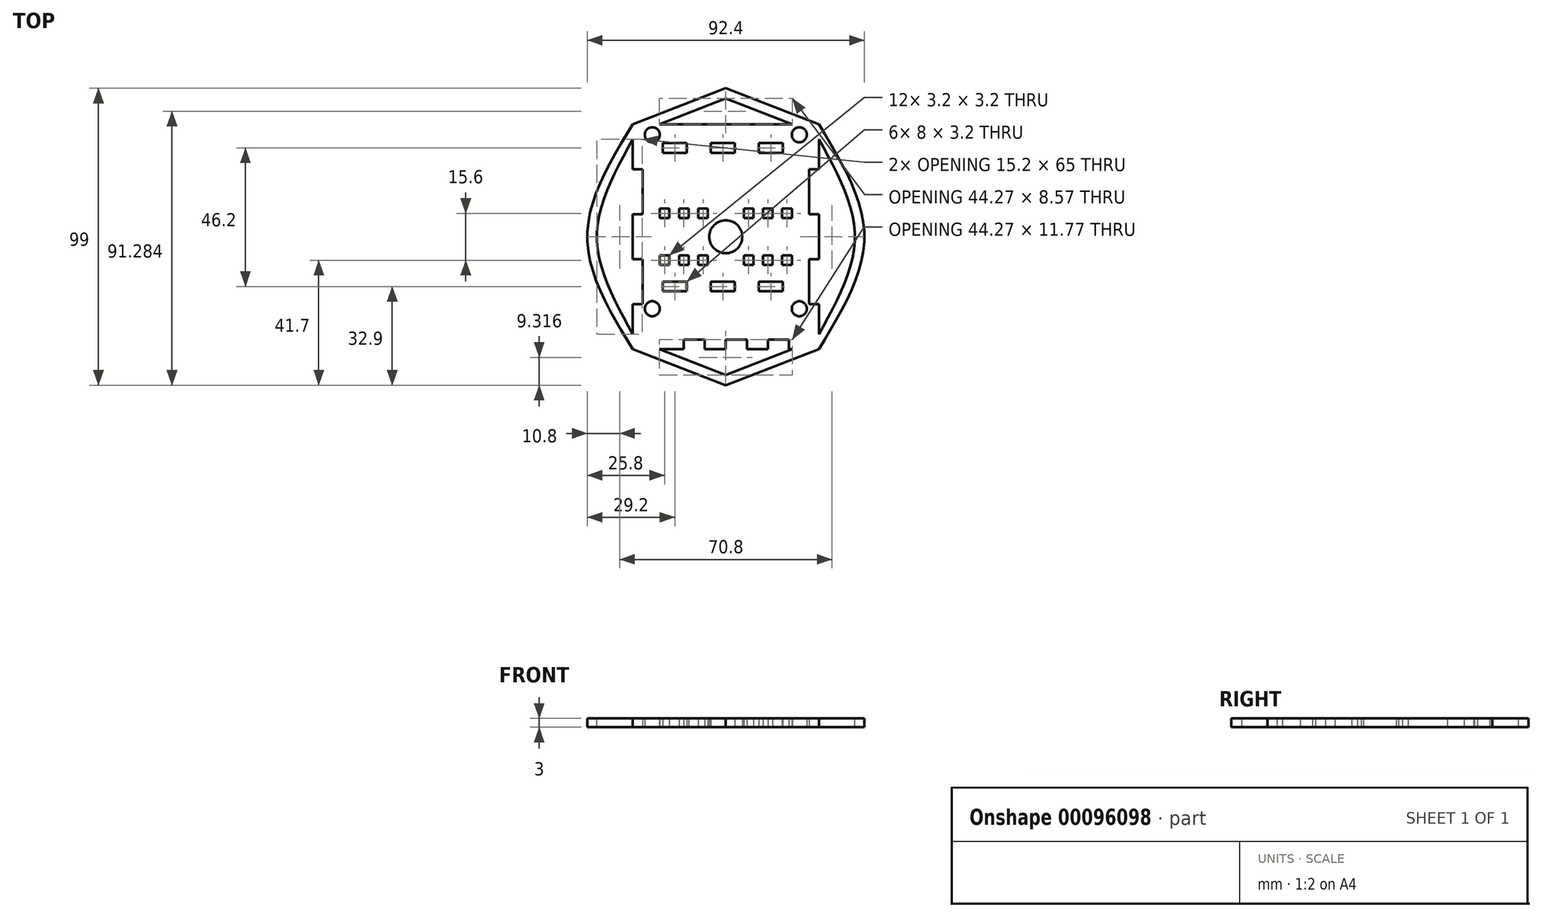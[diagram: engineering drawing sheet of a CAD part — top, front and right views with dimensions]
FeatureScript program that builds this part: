
annotation { "Feature Type Name" : "Feature", "Feature Type Description" : "" }
export const myFeature = defineFeature(function(context is Context, id is Id, definition is map)
    precondition{}
    {
        {
            var Q0;
            Q0=qCreatedBy(makeId("Top.planeOp"),FACE);
            var sketch = newSketch(context, id + "F0", { "sketchPlane" : qUnion([Q0])});
            skLineSegment(sketch, "E0.top", {"start": v(0, 37.5) * mm, "end": v(-22.14, 37.5) * mm});
            skLineSegment(sketch, "E0.right", {"start": v(-31, -32.5) * mm, "end": v(-31, -22.5) * mm});
            skPoint(sketch, "E0.middle", {"position": v(0, 0) * mm});
            skLineSegment(sketch, "E1", {"start": v(-31, 22.5) * mm, "end": v(-27.8, 22.5) * mm});
            skLineSegment(sketch, "E2", {"start": v(-27.8, 22.5) * mm, "end": v(-27.8, 7.5) * mm});
            skLineSegment(sketch, "E3", {"start": v(-27.8, 7.5) * mm, "end": v(-31, 7.5) * mm});
            skLineSegment(sketch, "E4", {"start": v(-31, 7.5) * mm, "end": v(-31, -7.5) * mm});
            skLineSegment(sketch, "E5", {"start": v(-31, -7.5) * mm, "end": v(-27.8, -7.5) * mm});
            skLineSegment(sketch, "E6", {"start": v(-27.8, -7.5) * mm, "end": v(-27.8, -22.5) * mm});
            skLineSegment(sketch, "E7", {"start": v(-27.8, -22.5) * mm, "end": v(-31, -22.5) * mm});
            skLineSegment(sketch, "E8", {"start": v(-31, -22.5) * mm, "end": v(-31, -32.5) * mm});
            skLineSegment(sketch, "E9", {"start": v(27.8, 22.5) * mm, "end": v(31, 22.5) * mm});
            skLineSegment(sketch, "E10", {"start": v(31, 7.5) * mm, "end": v(27.8, 7.5) * mm});
            skLineSegment(sketch, "E11", {"start": v(27.8, -7.5) * mm, "end": v(31, -7.5) * mm});
            skLineSegment(sketch, "E12", {"start": v(31, -22.5) * mm, "end": v(27.8, -22.5) * mm});
            skLineSegment(sketch, "E13.trimOffspring", {"start": v(-31, 22.5) * mm, "end": v(-31, 32.5) * mm});
            skLineSegment(sketch, "E14.trimOffspring", {"start": v(-31, -7.5) * mm, "end": v(-31, 7.5) * mm});
            skCircle(sketch, "E15", {"center": v(0, 0) * mm, "radius": 5.5 * mm});
            skLineSegment(sketch, "E16", {"start": v(0, 0) * mm, "end": v(5.5, 0) * mm, "construction": true});
            skLineSegment(sketch, "E17", {"start": v(-31, 0) * mm, "end": v(0, 0) * mm, "construction": true});
            skLineSegment(sketch, "E18", {"start": v(0, -14.47) * mm, "end": v(0, 12.75) * mm, "construction": true});
            skLineSegment(sketch, "E19", {"start": v(5.5, 0) * mm, "end": v(6, 0) * mm, "construction": true});
            skLineSegment(sketch, "E20", {"start": v(6, 0) * mm, "end": v(6, 9.4) * mm, "construction": true});
            skLineSegment(sketch, "E21.bottom", {"start": v(6, 9.4) * mm, "end": v(9.2, 9.4) * mm});
            skLineSegment(sketch, "E21.top", {"start": v(6, 6.2) * mm, "end": v(9.2, 6.2) * mm});
            skLineSegment(sketch, "E21.left", {"start": v(6, 9.4) * mm, "end": v(6, 6.2) * mm});
            skLineSegment(sketch, "E21.right", {"start": v(9.2, 9.4) * mm, "end": v(9.2, 6.2) * mm});
            skLineSegment(sketch, "E22", {"start": v(6, 0) * mm, "end": v(12.4, 0) * mm, "construction": true});
            skLineSegment(sketch, "E23", {"start": v(12.4, 0) * mm, "end": v(12.4, 9.4) * mm, "construction": true});
            skLineSegment(sketch, "E24", {"start": v(12.4, 0) * mm, "end": v(18.8, 0) * mm, "construction": true});
            skLineSegment(sketch, "E25", {"start": v(18.8, 0) * mm, "end": v(18.8, 9.4) * mm, "construction": true});
            skLineSegment(sketch, "E26", {"start": v(18.8, 0) * mm, "end": v(24, 0) * mm, "construction": true});
            skLineSegment(sketch, "E27.bottom", {"start": v(12.4, 9.4) * mm, "end": v(15.6, 9.4) * mm});
            skLineSegment(sketch, "E27.top", {"start": v(12.4, 6.2) * mm, "end": v(15.6, 6.2) * mm});
            skLineSegment(sketch, "E27.left", {"start": v(12.4, 9.4) * mm, "end": v(12.4, 6.2) * mm});
            skLineSegment(sketch, "E27.right", {"start": v(15.6, 9.4) * mm, "end": v(15.6, 6.2) * mm});
            skLineSegment(sketch, "E28.bottom", {"start": v(18.8, 9.4) * mm, "end": v(22, 9.4) * mm});
            skLineSegment(sketch, "E28.top", {"start": v(18.8, 6.2) * mm, "end": v(22, 6.2) * mm});
            skLineSegment(sketch, "E28.left", {"start": v(18.8, 9.4) * mm, "end": v(18.8, 6.2) * mm});
            skLineSegment(sketch, "E28.right", {"start": v(22, 9.4) * mm, "end": v(22, 6.2) * mm});
            skLineSegment(sketch, "E29.MirrorCS", {"start": v(-5.5, 0) * mm, "end": v(-6, 0) * mm, "construction": true});
            skLineSegment(sketch, "E30.MirrorCS", {"start": v(-6, 0) * mm, "end": v(-12.4, 0) * mm, "construction": true});
            skLineSegment(sketch, "E31.MirrorCS", {"start": v(-18.8, 0) * mm, "end": v(-24, 0) * mm, "construction": true});
            skLineSegment(sketch, "E32.MirrorCS", {"start": v(-12.4, 0) * mm, "end": v(-18.8, 0) * mm, "construction": true});
            skLineSegment(sketch, "E33", {"start": v(-31, 0) * mm, "end": v(27.8, 0) * mm, "construction": true});
            skLineSegment(sketch, "E34.MirrorCS", {"start": v(0, 0) * mm, "end": v(0, 30) * mm, "construction": true});
            skLineSegment(sketch, "E35.MirrorCS", {"start": v(6, -9.4) * mm, "end": v(9.2, -9.4) * mm});
            skLineSegment(sketch, "E36.MirrorCS", {"start": v(12.4, -9.4) * mm, "end": v(12.4, -6.2) * mm});
            skLineSegment(sketch, "E37.MirrorCS", {"start": v(18.8, -9.4) * mm, "end": v(18.8, -6.2) * mm});
            skLineSegment(sketch, "E38.MirrorCS", {"start": v(6, -9.4) * mm, "end": v(6, -6.2) * mm});
            skLineSegment(sketch, "E39.MirrorCS", {"start": v(18.8, -9.4) * mm, "end": v(22, -9.4) * mm});
            skLineSegment(sketch, "E40.MirrorCS", {"start": v(6, -6.2) * mm, "end": v(9.2, -6.2) * mm});
            skLineSegment(sketch, "E41.MirrorCS", {"start": v(12.4, 0) * mm, "end": v(12.4, -9.4) * mm, "construction": true});
            skLineSegment(sketch, "E42.MirrorCS", {"start": v(9.2, -9.4) * mm, "end": v(9.2, -6.2) * mm});
            skLineSegment(sketch, "E43.MirrorCS", {"start": v(15.6, -9.4) * mm, "end": v(15.6, -6.2) * mm});
            skLineSegment(sketch, "E44.MirrorCS", {"start": v(12.4, -6.2) * mm, "end": v(15.6, -6.2) * mm});
            skLineSegment(sketch, "E45.MirrorCS", {"start": v(12.4, -9.4) * mm, "end": v(15.6, -9.4) * mm});
            skLineSegment(sketch, "E46.MirrorCS", {"start": v(18.8, 0) * mm, "end": v(18.8, -9.4) * mm, "construction": true});
            skLineSegment(sketch, "E47.MirrorCS", {"start": v(18.8, -6.2) * mm, "end": v(22, -6.2) * mm});
            skLineSegment(sketch, "E48.MirrorCS", {"start": v(22, -9.4) * mm, "end": v(22, -6.2) * mm});
            skLineSegment(sketch, "E49.MirrorCS", {"start": v(6, 0) * mm, "end": v(6, -9.4) * mm, "construction": true});
            skLineSegment(sketch, "E50.MirrorCS", {"start": v(-9.2, 9.4) * mm, "end": v(-9.2, 6.2) * mm});
            skLineSegment(sketch, "E51.MirrorCS", {"start": v(-15.6, 9.4) * mm, "end": v(-15.6, 6.2) * mm});
            skLineSegment(sketch, "E52.MirrorCS", {"start": v(-12.4, 9.4) * mm, "end": v(-15.6, 9.4) * mm});
            skLineSegment(sketch, "E53.MirrorCS", {"start": v(-18.8, 6.2) * mm, "end": v(-22, 6.2) * mm});
            skLineSegment(sketch, "E54.MirrorCS", {"start": v(-18.8, 9.4) * mm, "end": v(-18.8, 6.2) * mm});
            skLineSegment(sketch, "E55.MirrorCS", {"start": v(-6, 9.4) * mm, "end": v(-9.2, 9.4) * mm});
            skLineSegment(sketch, "E56.MirrorCS", {"start": v(-22, 9.4) * mm, "end": v(-22, 6.2) * mm});
            skLineSegment(sketch, "E57.MirrorCS", {"start": v(-18.8, 9.4) * mm, "end": v(-22, 9.4) * mm});
            skLineSegment(sketch, "E58.MirrorCS", {"start": v(-6, 6.2) * mm, "end": v(-9.2, 6.2) * mm});
            skLineSegment(sketch, "E59.MirrorCS", {"start": v(-12.4, 9.4) * mm, "end": v(-12.4, 6.2) * mm});
            skLineSegment(sketch, "E60.MirrorCS", {"start": v(-12.4, 6.2) * mm, "end": v(-15.6, 6.2) * mm});
            skLineSegment(sketch, "E61.MirrorCS", {"start": v(-6, 9.4) * mm, "end": v(-6, 6.2) * mm});
            skLineSegment(sketch, "E62.MirrorCS", {"start": v(-18.8, -9.4) * mm, "end": v(-18.8, -6.2) * mm});
            skLineSegment(sketch, "E63.MirrorCS", {"start": v(-12.4, -9.4) * mm, "end": v(-12.4, -6.2) * mm});
            skLineSegment(sketch, "E64.MirrorCS", {"start": v(-6, -9.4) * mm, "end": v(-6, -6.2) * mm});
            skLineSegment(sketch, "E65.MirrorCS", {"start": v(-12.4, -9.4) * mm, "end": v(-15.6, -9.4) * mm});
            skLineSegment(sketch, "E66.MirrorCS", {"start": v(-18.8, -6.2) * mm, "end": v(-22, -6.2) * mm});
            skLineSegment(sketch, "E67.MirrorCS", {"start": v(-18.8, -9.4) * mm, "end": v(-22, -9.4) * mm});
            skLineSegment(sketch, "E68.MirrorCS", {"start": v(-12.4, -6.2) * mm, "end": v(-15.6, -6.2) * mm});
            skLineSegment(sketch, "E69.MirrorCS", {"start": v(-12.4, 0) * mm, "end": v(-12.4, -9.4) * mm, "construction": true});
            skLineSegment(sketch, "E70.MirrorCS", {"start": v(-18.8, 0) * mm, "end": v(-18.8, -9.4) * mm, "construction": true});
            skLineSegment(sketch, "E71.MirrorCS", {"start": v(-6, -9.4) * mm, "end": v(-9.2, -9.4) * mm});
            skLineSegment(sketch, "E72.MirrorCS", {"start": v(-6, 0) * mm, "end": v(-6, -9.4) * mm, "construction": true});
            skLineSegment(sketch, "E73.MirrorCS", {"start": v(-22, -9.4) * mm, "end": v(-22, -6.2) * mm});
            skLineSegment(sketch, "E74.MirrorCS", {"start": v(-9.2, -9.4) * mm, "end": v(-9.2, -6.2) * mm});
            skLineSegment(sketch, "E75.MirrorCS", {"start": v(-6, -6.2) * mm, "end": v(-9.2, -6.2) * mm});
            skLineSegment(sketch, "E76.MirrorCS", {"start": v(-15.6, -9.4) * mm, "end": v(-15.6, -6.2) * mm});
            skLineSegment(sketch, "E77", {"start": v(31, 32.5) * mm, "end": v(31, 22.5) * mm});
            skLineSegment(sketch, "E78", {"start": v(27.8, 22.5) * mm, "end": v(27.8, 7.5) * mm});
            skLineSegment(sketch, "E79", {"start": v(27.8, -7.5) * mm, "end": v(27.8, -22.5) * mm});
            skLineSegment(sketch, "E80.trimOffspring", {"start": v(31, -22.5) * mm, "end": v(31, -32.5) * mm});
            skLineSegment(sketch, "E81", {"start": v(31, 7.5) * mm, "end": v(31, -7.5) * mm});
            skLineSegment(sketch, "E82", {"start": v(31, 22.5) * mm, "end": v(34.2, 22.5) * mm});
            skLineSegment(sketch, "E83", {"start": v(0, 37.5) * mm, "end": v(0, 49.5) * mm, "construction": true});
            skPoint(sketch, "E83.startSnap0", {"position": v(0, 15) * mm});
            skLineSegment(sketch, "E84", {"start": v(0, 43.5) * mm, "end": v(34.2, 43.5) * mm, "construction": true});
            skLineSegment(sketch, "E85", {"start": v(0, 43.5) * mm, "end": v(-40.16, 43.5) * mm, "construction": true});
            skLineSegment(sketch, "E86", {"start": v(34.2, 37.5) * mm, "end": v(34.2, 43.5) * mm, "construction": true});
            skLineSegment(sketch, "E87", {"start": v(-31, 0) * mm, "end": v(-43, 0) * mm, "construction": true});
            skLineSegment(sketch, "E88", {"start": v(-27.8, 15) * mm, "end": v(-54.38, 15) * mm, "construction": true});
            skLineSegment(sketch, "E89", {"start": v(-27.8, -15) * mm, "end": v(-55.02, -15) * mm, "construction": true});
            skLineSegment(sketch, "E90", {"start": v(-31, 0) * mm, "end": v(-31, -20) * mm, "construction": true});
            skLineSegment(sketch, "E91", {"start": v(-31, 0) * mm, "end": v(-31, 20) * mm, "construction": true});
            skLineSegment(sketch, "E92", {"start": v(-31, 20) * mm, "end": v(-43, 20) * mm, "construction": true});
            skLineSegment(sketch, "E93", {"start": v(-43, 20) * mm, "end": v(-43, -20) * mm, "construction": true});
            skLineSegment(sketch, "E94", {"start": v(-31, -32.5) * mm, "end": v(-31, -28.4) * mm, "construction": true});
            skLineSegment(sketch, "E95", {"start": v(-21, -37.5) * mm, "end": v(-22.14, -37.5) * mm, "construction": true});
            skLineSegment(sketch, "E96", {"start": v(-22.14, -37.5) * mm, "end": v(-21, -37.5) * mm});
            skLineSegment(sketch, "E97", {"start": v(22.14, -37.5) * mm, "end": v(21, -37.5) * mm});
            skLineSegment(sketch, "E98", {"start": v(21, -37.5) * mm, "end": v(21, -34.3) * mm});
            skLineSegment(sketch, "E99", {"start": v(21, -34.3) * mm, "end": v(14, -34.3) * mm});
            skLineSegment(sketch, "E100", {"start": v(14, -34.3) * mm, "end": v(14, -37.5) * mm});
            skLineSegment(sketch, "E101", {"start": v(14, -37.5) * mm, "end": v(7, -37.5) * mm});
            skLineSegment(sketch, "E102", {"start": v(7, -37.5) * mm, "end": v(7, -34.3) * mm});
            skLineSegment(sketch, "E103", {"start": v(7, -34.3) * mm, "end": v(0, -34.3) * mm});
            skLineSegment(sketch, "E104", {"start": v(0, -34.3) * mm, "end": v(0, -37.5) * mm});
            skLineSegment(sketch, "E105", {"start": v(0, -37.5) * mm, "end": v(-7, -37.5) * mm});
            skLineSegment(sketch, "E106", {"start": v(-7, -37.5) * mm, "end": v(-7, -34.3) * mm});
            skLineSegment(sketch, "E107", {"start": v(-7, -34.3) * mm, "end": v(-14, -34.3) * mm});
            skLineSegment(sketch, "E108", {"start": v(-14, -34.3) * mm, "end": v(-14, -37.5) * mm});
            skLineSegment(sketch, "E109", {"start": v(-14, -37.5) * mm, "end": v(-21, -37.5) * mm});
            skLineSegment(sketch, "E110", {"start": v(-31, 37.5) * mm, "end": v(0, 49.5) * mm});
            skLineSegment(sketch, "E111", {"start": v(0, 49.5) * mm, "end": v(31, 37.5) * mm});
            skLineSegment(sketch, "E112", {"start": v(0, 49.5) * mm, "end": v(0, 46.3) * mm, "construction": true});
            skLineSegment(sketch, "E113", {"start": v(0, 46.07) * mm, "end": v(-22.14, 37.5) * mm, "construction": true});
            skLineSegment(sketch, "E114.MirrorCS", {"start": v(0, 46.07) * mm, "end": v(22.14, 37.5) * mm, "construction": true});
            skLineSegment(sketch, "E115", {"start": v(0, 46.07) * mm, "end": v(22.14, 37.5) * mm});
            skLineSegment(sketch, "E116", {"start": v(0, 46.07) * mm, "end": v(-22.14, 37.5) * mm});
            skPoint(sketch, "E117.orphan", {"position": v(27.8, 37.5) * mm});
            skLineSegment(sketch, "E118", {"start": v(0, 37.5) * mm, "end": v(22.14, 37.5) * mm});
            skLineSegment(sketch, "E119.MirrorCS", {"start": v(-31, -37.5) * mm, "end": v(0, -49.5) * mm});
            skLineSegment(sketch, "E120.MirrorCS", {"start": v(0, -49.5) * mm, "end": v(31, -37.5) * mm});
            skLineSegment(sketch, "E121.MirrorCS", {"start": v(0, -46.07) * mm, "end": v(-22.14, -37.5) * mm, "construction": true});
            skLineSegment(sketch, "E122.MirrorCS", {"start": v(0, -46.07) * mm, "end": v(22.14, -37.5) * mm, "construction": true});
            skLineSegment(sketch, "E123", {"start": v(-22.14, -37.5) * mm, "end": v(0, -46.07) * mm, "construction": true});
            skLineSegment(sketch, "E124", {"start": v(-22.14, -37.5) * mm, "end": v(0, -46.07) * mm});
            skLineSegment(sketch, "E125", {"start": v(0, -46.07) * mm, "end": v(22.14, -37.5) * mm});
            skLineSegment(sketch, "E126.trimOffspring", {"start": v(-31, -37.5) * mm, "end": v(-48.51, -37.5) * mm, "construction": true});
            skPoint(sketch, "E0.left.start.orphan", {"position": v(31, -37.5) * mm});
            skLineSegment(sketch, "E127", {"start": v(-43, 0) * mm, "end": v(-46.2, 0) * mm, "construction": true});
            skFitSpline(sketch, "E128", {"points": [v(-31, 37.5) * mm, v(-46.2, 0) * mm, v(-31, -37.5) * mm], "startDerivative": vector(-45.6, -75) * mm, "endDerivative": vector(45.6, -75) * mm});
            skFitSpline(sketch, "E129.MirrorCS", {"points": [v(31, 37.5) * mm, v(46.2, 0) * mm, v(31, -37.5) * mm], "startDerivative": vector(45.6, -75) * mm, "endDerivative": vector(-45.6, -75) * mm});
            skLineSegment(sketch, "E130", {"start": v(-31, 37.5) * mm, "end": v(31, 37.5) * mm, "construction": true});
            skLineSegment(sketch, "E131", {"start": v(-31, 37.5) * mm, "end": v(-31, 34.3) * mm, "construction": true});
            skLineSegment(sketch, "E132", {"start": v(-31, 34) * mm, "end": v(31, 34) * mm, "construction": true});
            skLineSegment(sketch, "E133", {"start": v(0, 34) * mm, "end": v(-24.5, 34) * mm, "construction": true});
            skLineSegment(sketch, "E134", {"start": v(-24.5, 34) * mm, "end": v(-24.5, -24) * mm, "construction": true});
            skLineSegment(sketch, "E135", {"start": v(24.5, 34) * mm, "end": v(24.5, -24) * mm, "construction": true});
            skLineSegment(sketch, "E136.MirrorCS", {"start": v(-13, 28) * mm, "end": v(-21, 28) * mm});
            skLineSegment(sketch, "E137.MirrorCS", {"start": v(-13, 28) * mm, "end": v(-5, 28) * mm, "construction": true});
            skLineSegment(sketch, "E138.MirrorCS", {"start": v(-5, 28) * mm, "end": v(-5, 31.2) * mm});
            skLineSegment(sketch, "E139.MirrorCS", {"start": v(3, 28) * mm, "end": v(-5, 28) * mm});
            skLineSegment(sketch, "E140.MirrorCS", {"start": v(3, 28) * mm, "end": v(11, 28) * mm, "construction": true});
            skLineSegment(sketch, "E141.MirrorCS", {"start": v(19, 28) * mm, "end": v(11, 28) * mm});
            skLineSegment(sketch, "E142.MirrorCS", {"start": v(-21, 28) * mm, "end": v(-21, 31.2) * mm});
            skLineSegment(sketch, "E143.MirrorCS", {"start": v(-13, 31.2) * mm, "end": v(-13, 28) * mm});
            skLineSegment(sketch, "E144.MirrorCS", {"start": v(-5, 31.2) * mm, "end": v(3, 31.2) * mm});
            skLineSegment(sketch, "E145.MirrorCS", {"start": v(3, 31.2) * mm, "end": v(3, 28) * mm});
            skLineSegment(sketch, "E146.MirrorCS", {"start": v(11, 28) * mm, "end": v(11, 31.2) * mm});
            skLineSegment(sketch, "E147.MirrorCS", {"start": v(19, 31.2) * mm, "end": v(19, 28) * mm});
            skLineSegment(sketch, "E148.MirrorCS", {"start": v(11, 31.2) * mm, "end": v(19, 31.2) * mm});
            skLineSegment(sketch, "E149.MirrorCS", {"start": v(0, 28) * mm, "end": v(21, 28) * mm, "construction": true});
            skLineSegment(sketch, "E150.MirrorCS", {"start": v(0, 28) * mm, "end": v(-21, 28) * mm, "construction": true});
            skLineSegment(sketch, "E151.MirrorCS", {"start": v(-21, 31.2) * mm, "end": v(-13, 31.2) * mm});
            skFitSpline(sketch, "E152", {"points": [v(-31, 32.5) * mm, v(-43, 0) * mm, v(-31, -32.5) * mm], "startDerivative": vector(-36, -65) * mm, "endDerivative": vector(36, -65) * mm});
            skLineSegment(sketch, "E153.trimOffspring", {"start": v(-31, 32.5) * mm, "end": v(-31, 22.5) * mm});
            skLineSegment(sketch, "E154", {"start": v(43, 0) * mm, "end": v(46.2, 0) * mm, "construction": true});
            skFitSpline(sketch, "E155", {"points": [v(31, -32.5) * mm, v(43, 0) * mm, v(31, 32.5) * mm], "startDerivative": vector(36, 65) * mm, "endDerivative": vector(-36, 65) * mm});
            skLineSegment(sketch, "E156", {"start": v(-27.8, -15) * mm, "end": v(27.8, -15) * mm, "construction": true});
            skLineSegment(sketch, "E157", {"start": v(0, -23.1) * mm, "end": v(-21.89, -23.1) * mm, "construction": true});
            skLineSegment(sketch, "E158", {"start": v(0, -23.1) * mm, "end": v(22.57, -23.1) * mm, "construction": true});
            skLineSegment(sketch, "E159.MirrorCS", {"start": v(-13, -18.2) * mm, "end": v(-21, -18.2) * mm});
            skLineSegment(sketch, "E160.MirrorCS", {"start": v(-21, -18.2) * mm, "end": v(-21, -15) * mm});
            skLineSegment(sketch, "E161.MirrorCS", {"start": v(-21, -15) * mm, "end": v(-13, -15) * mm});
            skLineSegment(sketch, "E162.MirrorCS", {"start": v(-13, -15) * mm, "end": v(-13, -18.2) * mm});
            skLineSegment(sketch, "E163.MirrorCS", {"start": v(-13, -18.2) * mm, "end": v(-5, -18.2) * mm, "construction": true});
            skLineSegment(sketch, "E164.MirrorCS", {"start": v(-5, -18.2) * mm, "end": v(-5, -15) * mm});
            skLineSegment(sketch, "E165.MirrorCS", {"start": v(-5, -15) * mm, "end": v(3, -15) * mm});
            skLineSegment(sketch, "E166.MirrorCS", {"start": v(3, -15) * mm, "end": v(3, -18.2) * mm});
            skLineSegment(sketch, "E167.MirrorCS", {"start": v(3, -18.2) * mm, "end": v(-5, -18.2) * mm});
            skLineSegment(sketch, "E168.MirrorCS", {"start": v(0, -18.2) * mm, "end": v(-21, -18.2) * mm, "construction": true});
            skLineSegment(sketch, "E169.MirrorCS", {"start": v(11, -18.2) * mm, "end": v(11, -15) * mm});
            skLineSegment(sketch, "E170.MirrorCS", {"start": v(19, -18.2) * mm, "end": v(11, -18.2) * mm});
            skLineSegment(sketch, "E171.MirrorCS", {"start": v(19, -15) * mm, "end": v(19, -18.2) * mm});
            skLineSegment(sketch, "E172.MirrorCS", {"start": v(11, -15) * mm, "end": v(19, -15) * mm});
            skCircle(sketch, "E173", {"center": v(24.5, -24) * mm, "radius": 2.5 * mm});
            skCircle(sketch, "E174", {"center": v(-24.5, -24) * mm, "radius": 2.5 * mm});
            skCircle(sketch, "E175", {"center": v(-24.5, 34) * mm, "radius": 2.5 * mm});
            skCircle(sketch, "E176", {"center": v(24.5, 34) * mm, "radius": 2.5 * mm});
            skSolve(sketch);
        }
        {
            var Q0;
            Q0 = qSketchRegion(id + "F0", true);
            extrude(context, id + "F1", {"entities" : qUnion([Q0]), "endBound" : BoundingType.SYMMETRIC, "depth" : 3 * mm});
        }
    });
